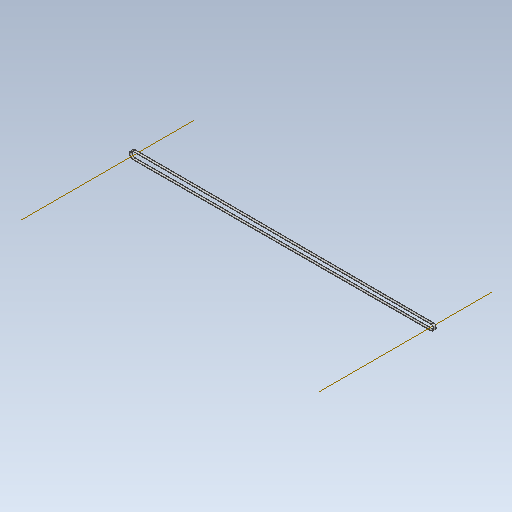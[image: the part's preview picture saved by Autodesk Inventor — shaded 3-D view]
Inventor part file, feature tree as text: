
AUTODESK INVENTOR PART (.ipt)
format: ipt  version: 2020 (Build 240168000, 168)  size: 92,672 bytes
history: native  units: mm (DEFAULTED — no unit token found)
features: other x4, plane x2, sketch x1, sweep x1
ambient origin geometry x8: Origin, YZ Plane, XZ Plane, XY Plane, X Axis, Y Axis, Z Axis, Center Point
bodies: Solid1 (feature_tree)
feature tree (8):
  sketch  "Sketch Path"  dims[d0=4.0mm d2=0.0mm d4=0.3mm d5=0.3mm d6=0.0mm d7=0.0mm d8=0.0mm d9=0.0mm d10=0.0mm d11=0.0mm]
  other  "Cross Section Plane"
  other  "Work Axis1"
  other  "Work Axis2"
  plane  "Work Plane2"
  plane  "Work Plane3"
  sweep  "Belt"
  other  "Cross Section"
